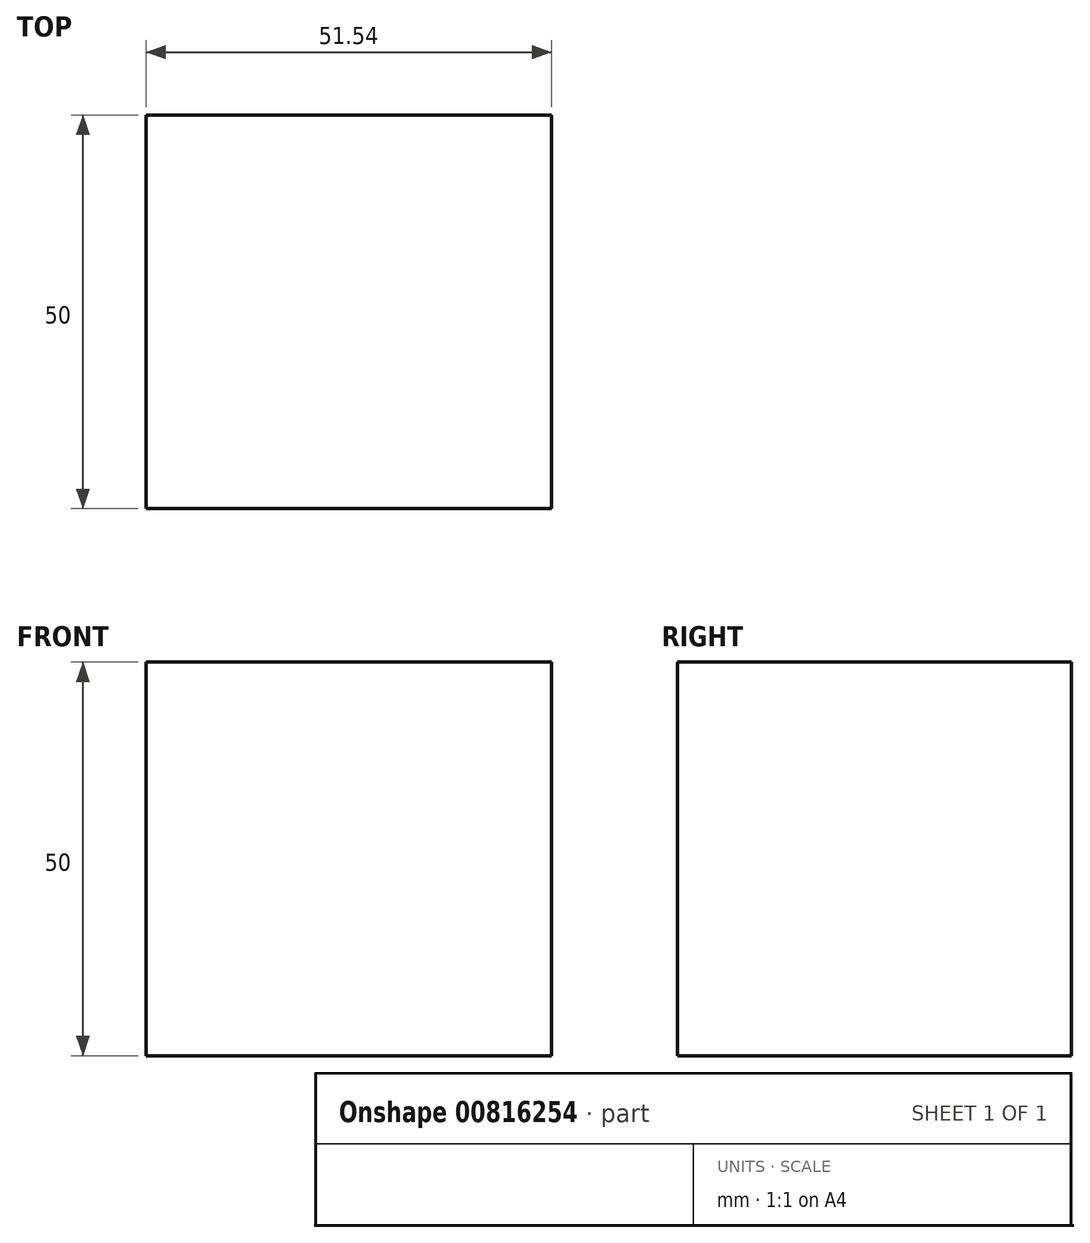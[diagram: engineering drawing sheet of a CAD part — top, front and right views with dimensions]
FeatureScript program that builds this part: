
annotation { "Feature Type Name" : "Feature", "Feature Type Description" : "" }
export const myFeature = defineFeature(function(context is Context, id is Id, definition is map)
    precondition{}
    {
        {
            var Q0;
            Q0=qCreatedBy(makeId("Top.planeOp"),FACE);
            var sketch = newSketch(context, id + "F0", { "sketchPlane" : qUnion([Q0])});
            skLineSegment(sketch, "E0.bottom", {"start": v(-24.92, 22.72) * mm, "end": v(26.62, 22.72) * mm});
            skLineSegment(sketch, "E0.top", {"start": v(-24.92, -27.28) * mm, "end": v(26.62, -27.28) * mm});
            skLineSegment(sketch, "E0.left", {"start": v(-24.92, 22.72) * mm, "end": v(-24.92, -27.28) * mm});
            skLineSegment(sketch, "E0.right", {"start": v(26.62, 22.72) * mm, "end": v(26.62, -27.28) * mm});
            skSolve(sketch);
        }
        {
            var Q0;
            Q0=makeQuery(id+"F0.imprint","IMPRINT",FACE,{"disambiguationData":[TD([[makeQuery(id+"F0.imprint","IMPRINT",EDGE,{"derivedFrom":sQuery(id+"F0.wireOp",EDGE,"E0.bottom")}),-1.0]])]});
            extrude(context, id + "F1", {"entities" : qUnion([Q0]), "depth" : 50 * mm, "offsetDistance" : 25 * mm});
        }
    });
